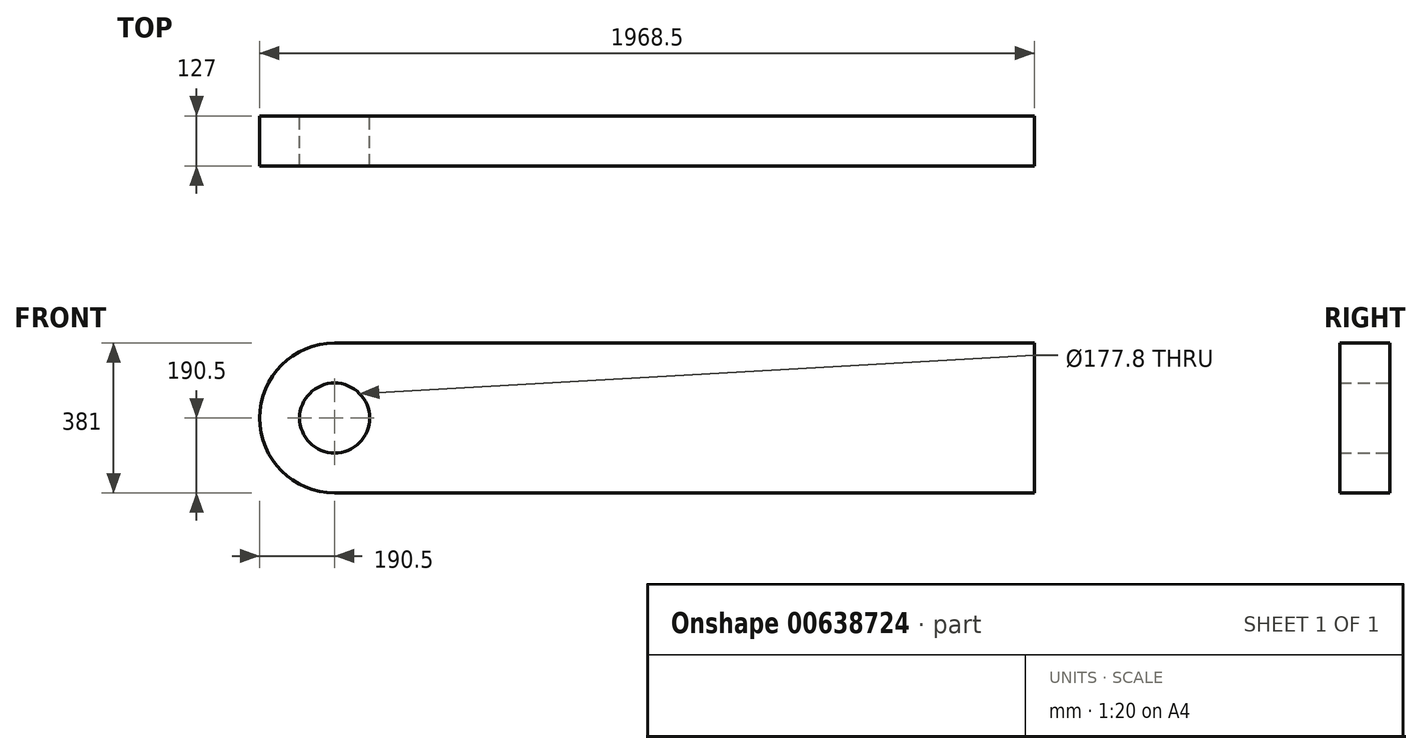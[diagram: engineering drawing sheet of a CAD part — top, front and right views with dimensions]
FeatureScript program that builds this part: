
annotation { "Feature Type Name" : "Feature", "Feature Type Description" : "" }
export const myFeature = defineFeature(function(context is Context, id is Id, definition is map)
    precondition{}
    {
        {
            var Q0;
            Q0=qCreatedBy(makeId("Front.planeOp"),FACE);
            var sketch = newSketch(context, id + "F0", { "sketchPlane" : qUnion([Q0])});
            skArc(sketch, "E0", {"start": v(-1778, 190.5) * mm, "mid": v(-1968.5, 0) * mm, "end": v(-1778, -190.5) * mm});
            skCircle(sketch, "E1", {"center": v(-1778, 0) * mm, "radius": 88.9 * mm});
            skLineSegment(sketch, "E2", {"start": v(-1778, 190.5) * mm, "end": v(0, 190.5) * mm});
            skLineSegment(sketch, "E3", {"start": v(-1778, -190.5) * mm, "end": v(0, -190.5) * mm});
            skLineSegment(sketch, "E4", {"start": v(0, -190.5) * mm, "end": v(0, 190.5) * mm});
            skSolve(sketch);
        }
        {
            var Q0;
            Q0=makeQuery(id+"F0.imprint","IMPRINT",FACE,{"disambiguationData":[TD([[makeQuery(id+"F0.imprint","IMPRINT",EDGE,{"derivedFrom":sQuery(id+"F0.wireOp",EDGE,"E0")}),1.0]])]});
            extrude(context, id + "F1", {"entities" : qUnion([Q0]), "depth" : 127 * mm, "offsetDistance" : 25.4 * mm});
        }
    });
